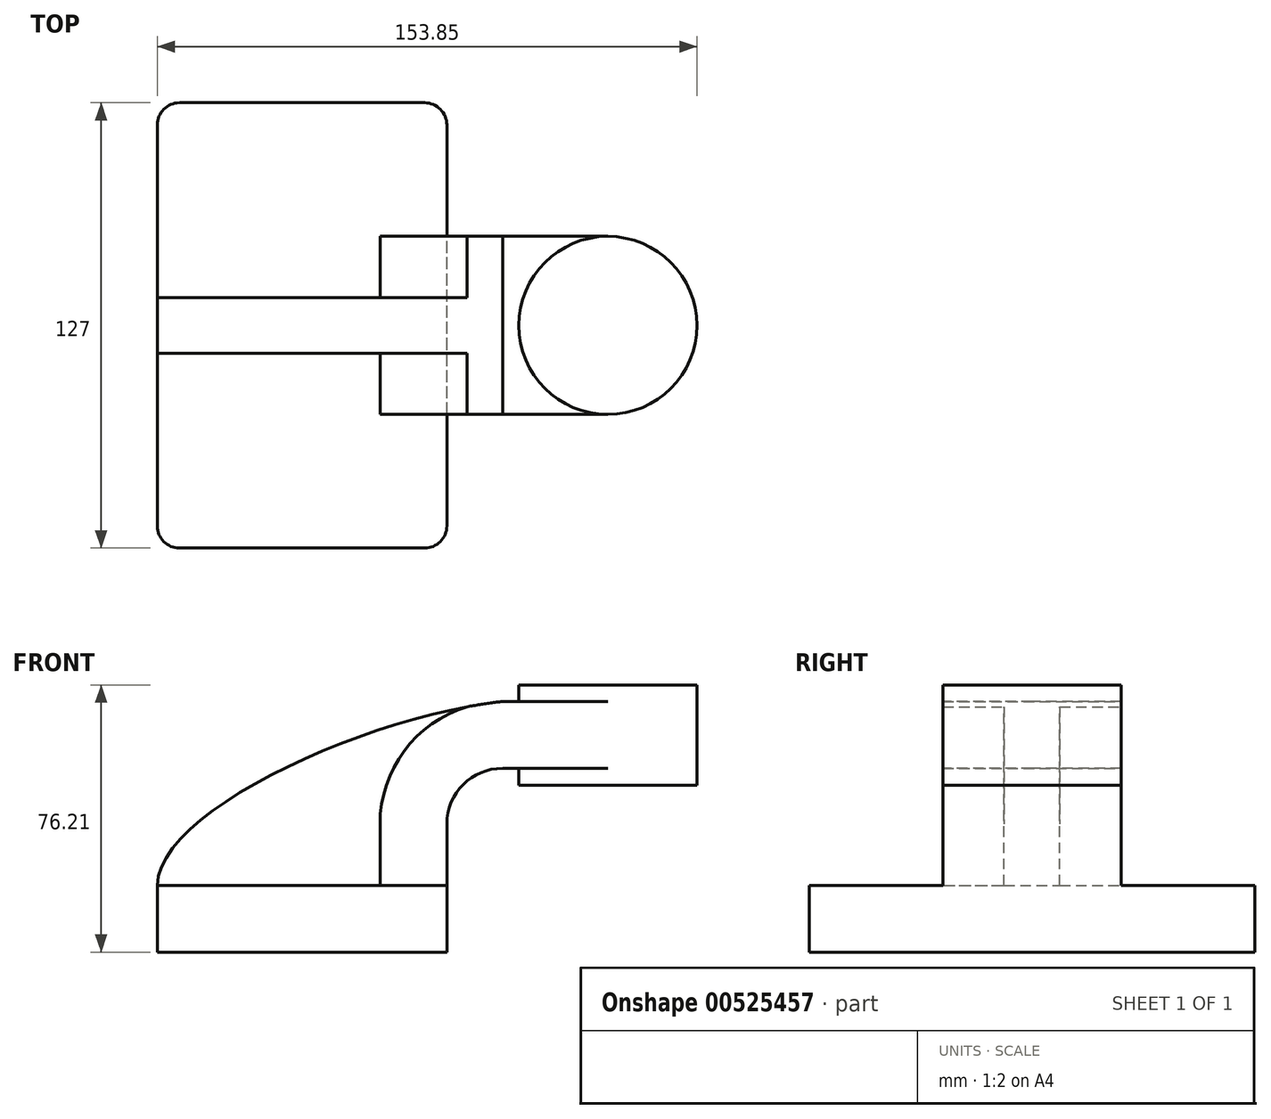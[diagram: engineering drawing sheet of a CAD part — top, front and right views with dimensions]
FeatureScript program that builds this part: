
annotation { "Feature Type Name" : "Feature", "Feature Type Description" : "" }
export const myFeature = defineFeature(function(context is Context, id is Id, definition is map)
    precondition{}
    {
        {
            var Q0;
            Q0=qCreatedBy(makeId("Front.planeOp"),FACE);
            var sketch = newSketch(context, id + "F0", { "sketchPlane" : qUnion([Q0])});
            skLineSegment(sketch, "E0.bottom", {"start": v(-41.28, 9.52) * mm, "end": v(41.28, 9.52) * mm});
            skLineSegment(sketch, "E0.top", {"start": v(-41.28, -9.52) * mm, "end": v(41.28, -9.52) * mm});
            skLineSegment(sketch, "E0.left", {"start": v(-41.28, 9.52) * mm, "end": v(-41.28, -9.52) * mm});
            skLineSegment(sketch, "E0.right", {"start": v(41.28, 9.52) * mm, "end": v(41.28, -9.52) * mm});
            skPoint(sketch, "E0.middle", {"position": v(0, 0) * mm});
            skLineSegment(sketch, "E1.bottom", {"start": v(112.57, 66.68) * mm, "end": v(61.77, 66.68) * mm});
            skLineSegment(sketch, "E1.top", {"start": v(112.57, 38.1) * mm, "end": v(61.77, 38.1) * mm});
            skLineSegment(sketch, "E1.left", {"start": v(112.57, 66.68) * mm, "end": v(112.57, 38.1) * mm});
            skLineSegment(sketch, "E1.right", {"start": v(61.77, 66.68) * mm, "end": v(61.77, 38.1) * mm});
            skPoint(sketch, "E1.middle", {"position": v(87.17, 52.39) * mm});
            skLineSegment(sketch, "E2", {"start": v(41.28, 9.52) * mm, "end": v(41.28, 27) * mm});
            skArc(sketch, "E3", {"start": v(41.28, 27) * mm, "mid": v(45.92, 38.23) * mm, "end": v(57.15, 42.88) * mm});
            skLineSegment(sketch, "E4", {"start": v(57.15, 42.88) * mm, "end": v(87.17, 42.88) * mm});
            skPoint(sketch, "E4.endSnap0", {"position": v(87.17, 38.1) * mm});
            skLineSegment(sketch, "E5.0", {"start": v(57.15, 61.93) * mm, "end": v(87.17, 61.93) * mm});
            skArc(sketch, "E5.1", {"start": v(22.23, 27) * mm, "mid": v(32.45, 51.7) * mm, "end": v(57.15, 61.93) * mm});
            skLineSegment(sketch, "E5.2", {"start": v(22.23, 9.52) * mm, "end": v(22.23, 27) * mm});
            skLineSegment(sketch, "E6", {"start": v(87.17, 38.1) * mm, "end": v(87.17, 66.68) * mm});
            skFitSpline(sketch, "E7", {"points": [v(-41.28, 9.52) * mm, v(57.15, 61.93) * mm], "startDerivative": vector(1.4, 64.34) * mm, "endDerivative": vector(115.23, 12.11) * mm});
            skSolve(sketch);
        }
        {
            var Q0;
            Q0=makeQuery(id+"F0.imprint","IMPRINT",FACE,{"disambiguationData":[TD([[makeQuery(id+"F0.imprint","IMPRINT",EDGE,{"derivedFrom":sQuery(id+"F0.wireOp",EDGE,"E0.top")}),1.0]])]});
            extrude(context, id + "F1", {"entities" : qUnion([Q0]), "endBound" : BoundingType.SYMMETRIC, "depth" : 127 * mm, "offsetDistance" : 25.4 * mm});
        }
        {
            var Q0;
            {var subQ1=sQuery(id+"F0.wireOp",EDGE,"E2");Q0=makeQuery(id+"F0.imprint","IMPRINT",FACE,{"disambiguationData":[TD([[makeQuery(id+"F0.imprint","IMPRINT",EDGE,{"derivedFrom":subQ1}),1.0]])]});}
            var Q1;
            {var subQ0=sQuery(id+"F0.wireOp",EDGE,"E5.0");var subQ1=sQuery(id+"F0.wireOp",EDGE,"E1.right");var subQ2=makeQuery(id+"F0.imprint","INTERSECT",VERTEX,{"derivedFrom":[subQ1,subQ0]});Q1=makeQuery(id+"F0.imprint","IMPRINT",FACE,{"disambiguationData":[TD([[makeQuery(id+"F0.imprint","IMPRINT",EDGE,{"disambiguationData":[TD([[subQ2,-1.0]])],"derivedFrom":subQ1}),1.0]])]});}
            extrude(context, id + "F2", {"entities" : qUnion([Q0, Q1]), "operationType" : NewBodyOperationType.ADD, "endBound" : BoundingType.SYMMETRIC, "depth" : 50.8 * mm, "offsetDistance" : 25.4 * mm});
        }
        {
            var Q0;
            {var subQ3=sQuery(id+"F0.wireOp",EDGE,"E5.2");Q0=makeQuery(id+"F0.imprint","IMPRINT",FACE,{"disambiguationData":[TD([[makeQuery(id+"F0.imprint","IMPRINT",EDGE,{"derivedFrom":subQ3}),1.0]])]});}
            extrude(context, id + "F3", {"entities" : qUnion([Q0]), "operationType" : NewBodyOperationType.ADD, "endBound" : BoundingType.SYMMETRIC, "depth" : 15.88 * mm, "offsetDistance" : 25.4 * mm});
        }
        {
            var Q0;
            {var subQ0=sQuery(id+"F0.wireOp",EDGE,"E1.left");Q0=makeQuery(id+"F0.imprint","IMPRINT",FACE,{"disambiguationData":[TD([[makeQuery(id+"F0.imprint","IMPRINT",EDGE,{"derivedFrom":subQ0}),-1.0]])]});}
            var Q1;
            Q1=sQuery(id+"F0.wireOp",EDGE,"E6");
            revolve(context, id + "F4", {"operationType" : NewBodyOperationType.ADD, "entities" : qUnion([Q0]), "axis" : qUnion([Q1]), "revolveType" : RevolveType.FULL});
        }
        {
            var Q0;
            Q0=makeQuery(id+"F1.opExtrude","CAP_EDGE",EDGE,{"disambiguationData":[OSD([sQuery(id+"F0.wireOp",EDGE,"E0.left")])],"isStart":true});
            var Q1;
            Q1=makeQuery(id+"F1.opExtrude","CAP_EDGE",EDGE,{"disambiguationData":[OSD([sQuery(id+"F0.wireOp",EDGE,"E0.right")])],"isStart":true});
            var Q2;
            Q2=makeQuery(id+"F1.opExtrude","CAP_EDGE",EDGE,{"disambiguationData":[OSD([sQuery(id+"F0.wireOp",EDGE,"E0.left")])],"isStart":false});
            var Q3;
            Q3=makeQuery(id+"F1.opExtrude","CAP_EDGE",EDGE,{"disambiguationData":[OSD([sQuery(id+"F0.wireOp",EDGE,"E0.right")])],"isStart":false});
            fillet(context, id + "F5", {"entities" : qUnion([Q0, Q1, Q2, Q3]), "radius" : 6.35 * mm, "tangentPropagation" : true, "allowEdgeOverflow" : false});
        }
    });
